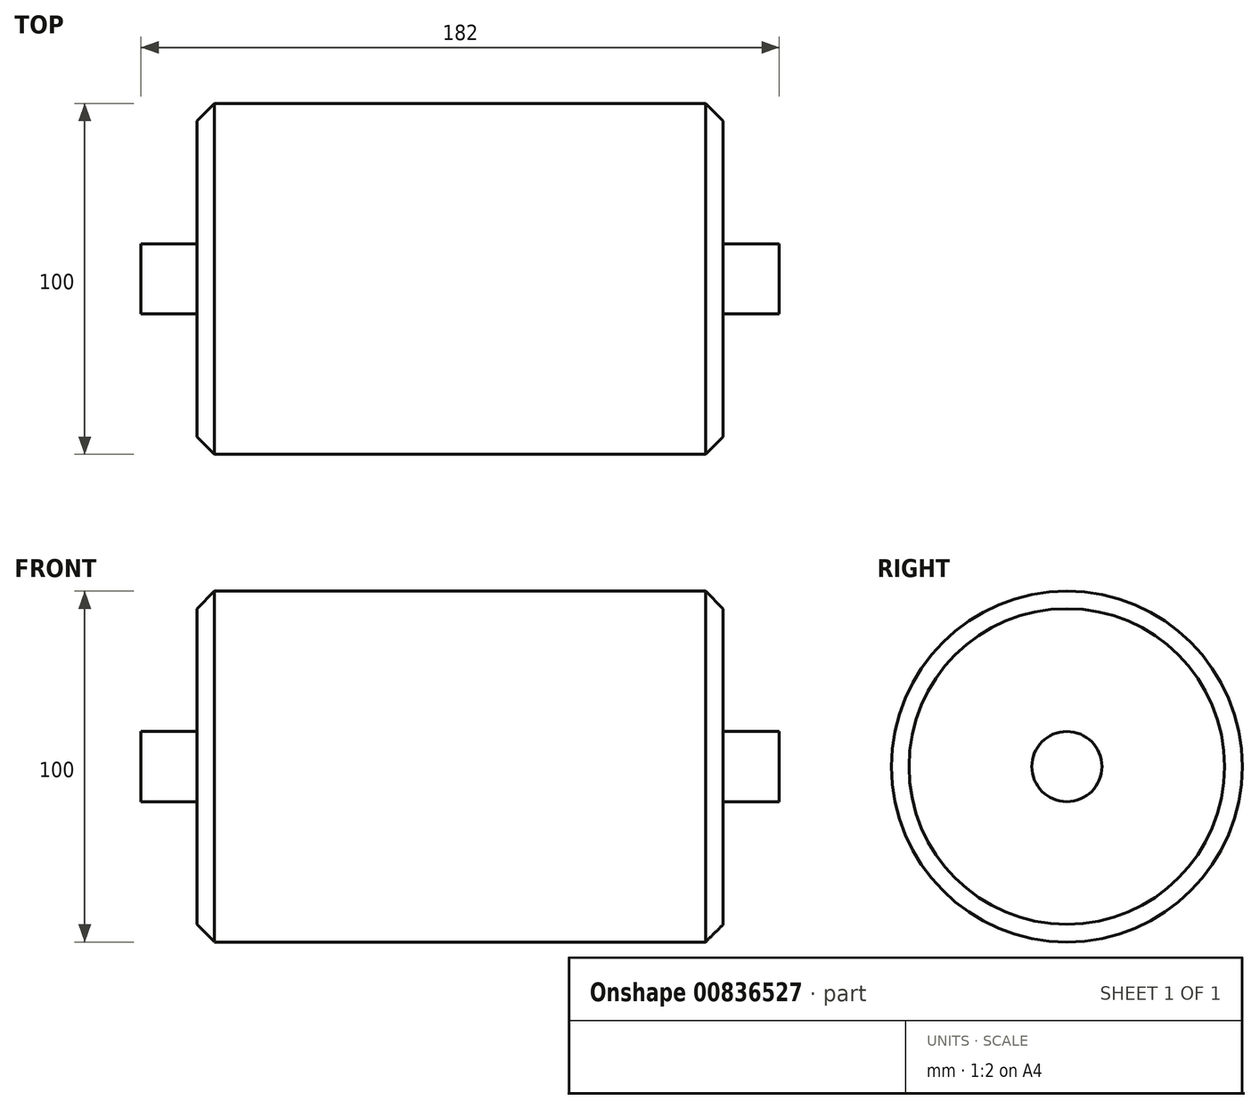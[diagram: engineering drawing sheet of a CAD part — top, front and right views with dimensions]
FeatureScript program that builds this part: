
annotation { "Feature Type Name" : "Feature", "Feature Type Description" : "" }
export const myFeature = defineFeature(function(context is Context, id is Id, definition is map)
    precondition{}
    {
        {
            var Q0;
            Q0=qCreatedBy(makeId("Top.planeOp"),FACE);
            var sketch = newSketch(context, id + "F0", { "sketchPlane" : qUnion([Q0])});
            skLineSegment(sketch, "E0", {"start": v(0, 0) * mm, "end": v(0, 50) * mm});
            skLineSegment(sketch, "E1", {"start": v(0, 50) * mm, "end": v(-75, 50) * mm});
            skLineSegment(sketch, "E2", {"start": v(-75, 50) * mm, "end": v(-75, 10) * mm});
            skLineSegment(sketch, "E3", {"start": v(-75, 10) * mm, "end": v(-91, 10) * mm});
            skLineSegment(sketch, "E4", {"start": v(-91, 10) * mm, "end": v(-91, 0) * mm});
            skLineSegment(sketch, "E5", {"start": v(-91, 0) * mm, "end": v(0, 0) * mm});
            skLineSegment(sketch, "E6.MirrorCS", {"start": v(75, 10) * mm, "end": v(91, 10) * mm});
            skLineSegment(sketch, "E7.MirrorCS", {"start": v(0, 50) * mm, "end": v(75, 50) * mm});
            skLineSegment(sketch, "E8.MirrorCS", {"start": v(91, 0) * mm, "end": v(0, 0) * mm});
            skLineSegment(sketch, "E9.MirrorCS", {"start": v(91, 10) * mm, "end": v(91, 0) * mm});
            skLineSegment(sketch, "E10.MirrorCS", {"start": v(75, 50) * mm, "end": v(75, 10) * mm});
            skSolve(sketch);
        }
        {
            var Q0;
            Q0 = qSketchRegion(id + "F0", true);
            var Q1;
            Q1=sQuery(id+"F0.wireOp",EDGE,"E5");
            revolve(context, id + "F1", {"surfaceOperationType" : NewSurfaceOperationType.NEW, "entities" : qUnion([Q0]), "axis" : qUnion([Q1]), "revolveType" : RevolveType.FULL});
        }
        {
            var Q0;
            Q0=makeQuery(id+"F1.opRevolve","SWEPT_EDGE",EDGE,{"disambiguationData":[OSD([sQuery(id+"F0.wireOp",EDGE,"E1"),sQuery(id+"F0.wireOp",EDGE,"E2")])]});
            var Q1;
            Q1=makeQuery(id+"F1.opRevolve","SWEPT_EDGE",EDGE,{"disambiguationData":[OSD([sQuery(id+"F0.wireOp",EDGE,"E7.MirrorCS"),sQuery(id+"F0.wireOp",EDGE,"E10.MirrorCS")])]});
            chamfer(context, id + "F2", {"entities" : qUnion([Q0, Q1]), "width" : 5 * mm, "tangentPropagation" : true});
        }
    });
